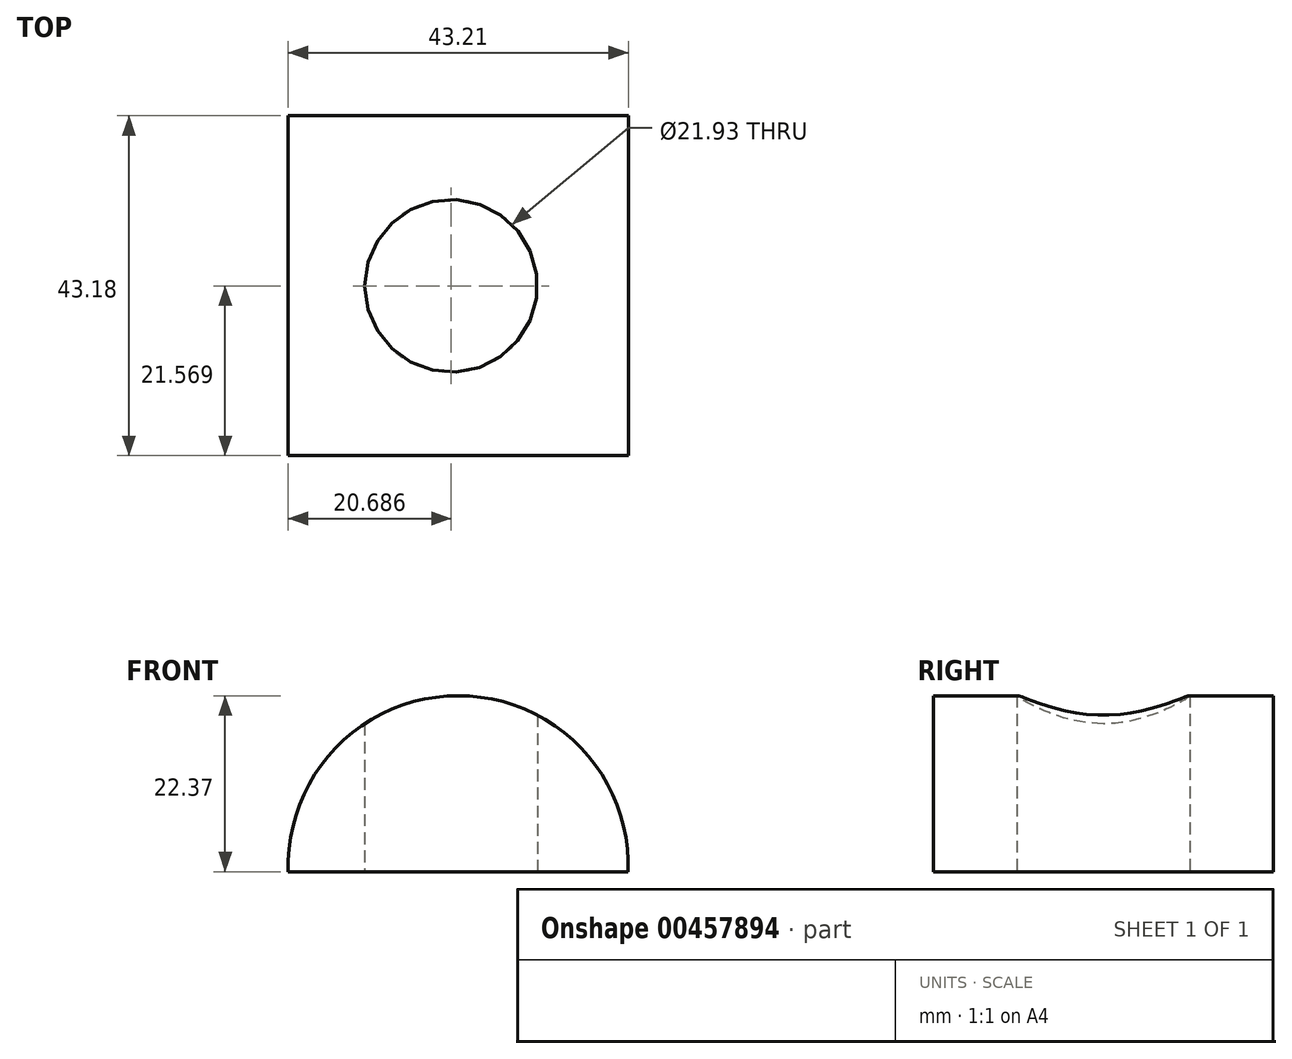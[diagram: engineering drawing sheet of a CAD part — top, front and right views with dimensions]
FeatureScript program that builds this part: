
annotation { "Feature Type Name" : "Feature", "Feature Type Description" : "" }
export const myFeature = defineFeature(function(context is Context, id is Id, definition is map)
    precondition{}
    {
        {
            var Q0;
            Q0=qCreatedBy(makeId("Front.planeOp"),FACE);
            var sketch = newSketch(context, id + "F0", { "sketchPlane" : qUnion([Q0])});
            skLineSegment(sketch, "E0", {"start": v(-60.48, 0) * mm, "end": v(-17.3, 0) * mm});
            skArc(sketch, "E1", {"start": v(-17.3, 0) * mm, "mid": v(-38.89, 22.37) * mm, "end": v(-60.48, 0) * mm});
            skSolve(sketch);
        }
        {
            var Q0;
            Q0 = qSketchRegion(id + "F0", true);
            extrude(context, id + "F1", {"entities" : qUnion([Q0]), "depth" : 43.18 * mm});
        }
        {
            var Q0;
            Q0=qCreatedBy(makeId("Top.planeOp"),FACE);
            var sketch = newSketch(context, id + "F2", { "sketchPlane" : qUnion([Q0])});
            skLineSegment(sketch, "E2", {"start": v(-39.8, -43.22) * mm, "end": v(-39.8, 0) * mm, "construction": true});
            skCircle(sketch, "E3", {"center": v(-39.8, -21.61) * mm, "radius": 10.96 * mm});
            skSolve(sketch);
        }
        {
            var Q0;
            Q0=makeQuery(id+"F2.imprint","IMPRINT",FACE,{"disambiguationData":[TD([[makeQuery(id+"F2.imprint","IMPRINT",EDGE,{"derivedFrom":sQuery(id+"F2.wireOp",EDGE,"E3")}),1.0]])]});
            extrude(context, id + "F3", {"entities" : qUnion([Q0]), "operationType" : NewBodyOperationType.REMOVE, "endBound" : BoundingType.THROUGH_ALL, "depth" : 25.4 * mm});
        }
    });
